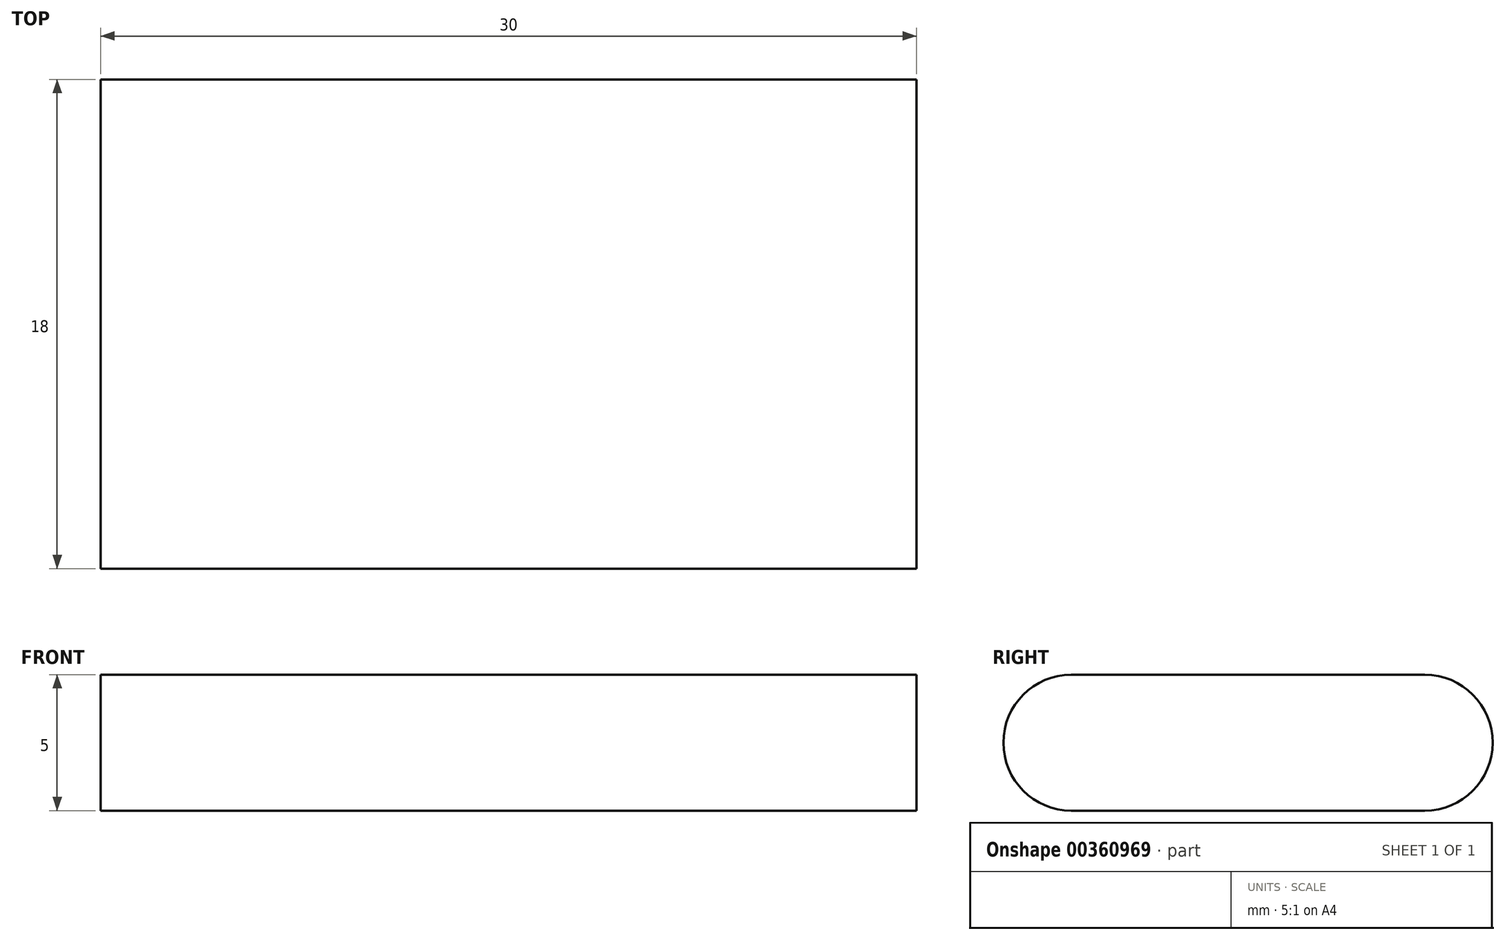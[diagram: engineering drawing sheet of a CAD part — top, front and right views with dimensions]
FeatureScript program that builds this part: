
annotation { "Feature Type Name" : "Feature", "Feature Type Description" : "" }
export const myFeature = defineFeature(function(context is Context, id is Id, definition is map)
    precondition{}
    {
        {
            var Q0;
            Q0=qCreatedBy(makeId("Right.planeOp"),FACE);
            var sketch = newSketch(context, id + "F0", { "sketchPlane" : qUnion([Q0])});
            skLineSegment(sketch, "E0.bottom", {"start": v(6.5, 2.5) * mm, "end": v(-6.5, 2.5) * mm});
            skLineSegment(sketch, "E0.top", {"start": v(6.5, -2.5) * mm, "end": v(-6.5, -2.5) * mm});
            skLineSegment(sketch, "E0.left", {"start": v(9, 0) * mm, "end": v(9, 0) * mm});
            skLineSegment(sketch, "E0.right", {"start": v(-9, 0) * mm, "end": v(-9, 0) * mm});
            skPoint(sketch, "E0.middle", {"position": v(0, 0) * mm});
            skPoint(sketch, "E1.visualSharp", {"position": v(-9, 2.5) * mm});
            skArc(sketch, "E1.filletArc", {"start": v(-6.5, 2.5) * mm, "mid": v(-8.27, 1.77) * mm, "end": v(-9, 0) * mm});
            skPoint(sketch, "E2.visualSharp", {"position": v(9, 2.5) * mm});
            skArc(sketch, "E2.filletArc", {"start": v(9, 0) * mm, "mid": v(8.27, 1.77) * mm, "end": v(6.5, 2.5) * mm});
            skPoint(sketch, "E3.visualSharp", {"position": v(9, -2.5) * mm});
            skArc(sketch, "E3.filletArc", {"start": v(6.5, -2.5) * mm, "mid": v(8.27, -1.77) * mm, "end": v(9, 0) * mm});
            skPoint(sketch, "E4.visualSharp", {"position": v(-9, -2.5) * mm});
            skArc(sketch, "E4.filletArc", {"start": v(-9, 0) * mm, "mid": v(-8.27, -1.77) * mm, "end": v(-6.5, -2.5) * mm});
            skSolve(sketch);
        }
        {
            var Q0;
            Q0=makeQuery(id+"F0.imprint","IMPRINT",FACE,{"disambiguationData":[TD([[makeQuery(id+"F0.imprint","IMPRINT",EDGE,{"derivedFrom":sQuery(id+"F0.wireOp",EDGE,"E0.bottom")}),1.0]])]});
            extrude(context, id + "F1", {"entities" : qUnion([Q0]), "endBound" : BoundingType.SYMMETRIC, "depth" : 30 * mm});
        }
    });
